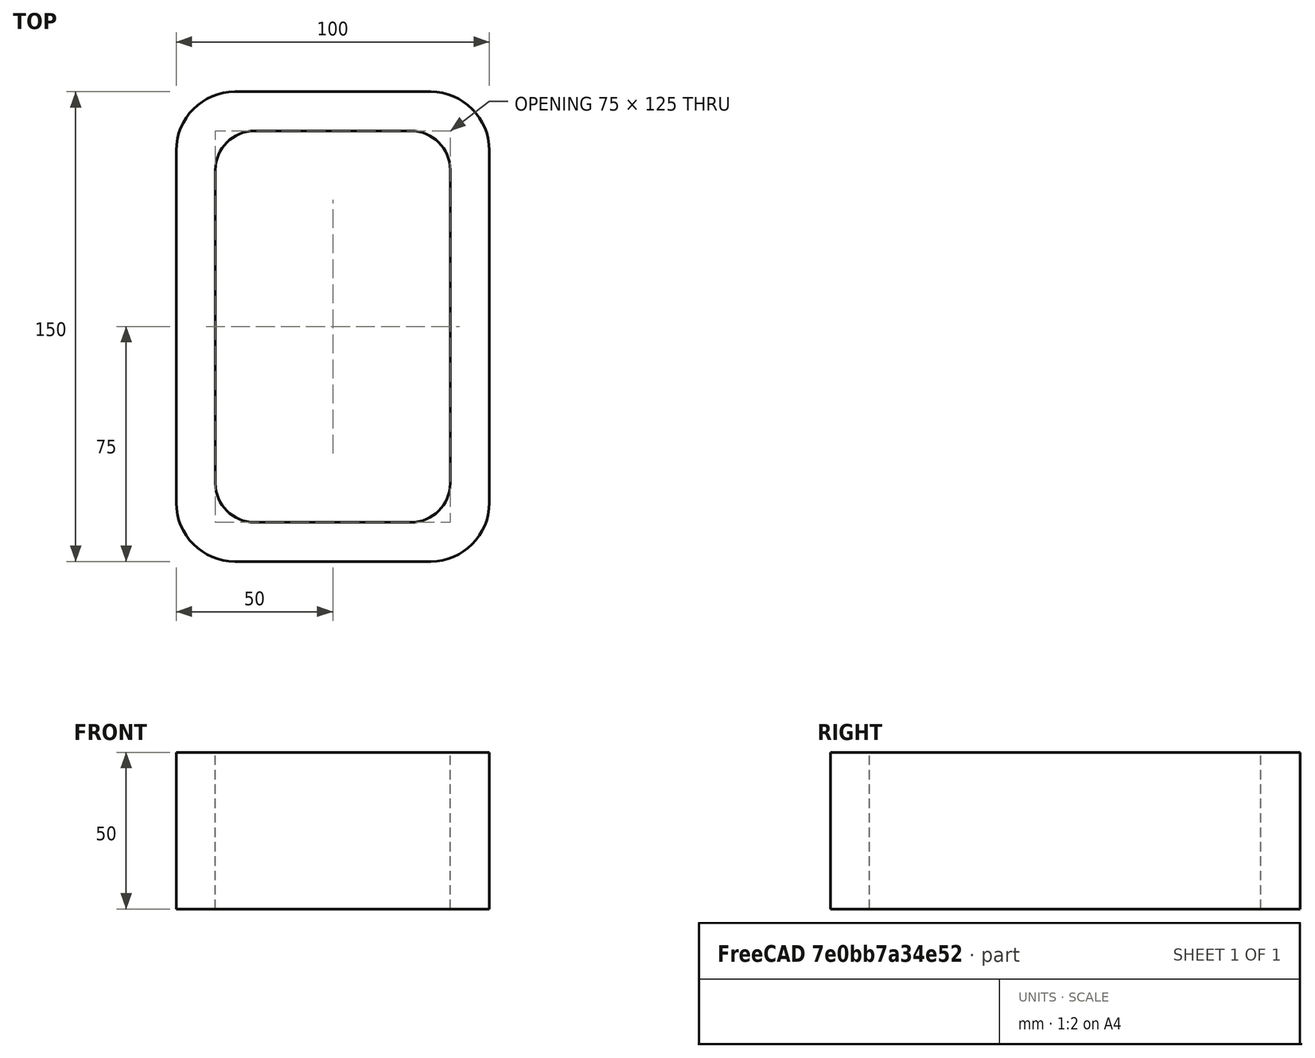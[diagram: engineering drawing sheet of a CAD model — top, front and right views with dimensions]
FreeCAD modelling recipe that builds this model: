
FCSTD DOCUMENT  (FreeCAD 0.15R4671 (Git))
Label: Rectangular hollow section 150x100x12.5 EN10219 S235JRH
License: All rights reserved
LicenseURL: http://en.wikipedia.org/wiki/All_rights_reserved
objects: Sketcher::SketchObject×1, Part::Extrusion×1
note: 2 computed .brp shape members not serialized (recipe doc carries the construction recipe); baked Part::Feature solids carry a one-line shape summary decoded from their .brp

FEATURE [Sketcher::SketchObject] Sketch
  sketch-geometry (16):
    g0: LineSegment StartX=-25 StartY=62.5 StartZ=0 EndX=25 EndY=62.5 EndZ=0
    g1: LineSegment StartX=37.5 StartY=50 StartZ=0 EndX=37.5 EndY=-50 EndZ=0
    g2: LineSegment StartX=25 StartY=-62.5 StartZ=0 EndX=-25 EndY=-62.5 EndZ=0
    g3: LineSegment StartX=-37.5 StartY=-50 StartZ=0 EndX=-37.5 EndY=50 EndZ=0
    g4: LineSegment StartX=-31.25 StartY=75 StartZ=0 EndX=31.25 EndY=75 EndZ=0
    g5: LineSegment StartX=50 StartY=56.25 StartZ=0 EndX=50 EndY=-56.25 EndZ=0
    g6: LineSegment StartX=31.25 StartY=-75 StartZ=0 EndX=-31.25 EndY=-75 EndZ=0
    g7: LineSegment StartX=-50 StartY=-56.25 StartZ=0 EndX=-50 EndY=56.25 EndZ=0
    g8: ArcOfCircle CenterX=-25 CenterY=50 CenterZ=0 NormalX=0 NormalY=0 NormalZ=1 Radius=12.5 StartAngle=1.5708 EndAngle=3.14159
    g9: ArcOfCircle CenterX=25 CenterY=50 CenterZ=0 NormalX=0 NormalY=0 NormalZ=1 Radius=12.5 StartAngle=0 EndAngle=1.5708
    g10: ArcOfCircle CenterX=25 CenterY=-50 CenterZ=0 NormalX=0 NormalY=0 NormalZ=1 Radius=12.5 StartAngle=4.71239 EndAngle=6.28319
    g11: ArcOfCircle CenterX=-25 CenterY=-50 CenterZ=0 NormalX=0 NormalY=0 NormalZ=1 Radius=12.5 StartAngle=3.14159 EndAngle=4.71239
    g12: ArcOfCircle CenterX=31.25 CenterY=56.25 CenterZ=0 NormalX=0 NormalY=0 NormalZ=1 Radius=18.75 StartAngle=0 EndAngle=1.5708
    g13: ArcOfCircle CenterX=31.25 CenterY=-56.25 CenterZ=0 NormalX=0 NormalY=0 NormalZ=1 Radius=18.75 StartAngle=4.71239 EndAngle=6.28319
    g14: ArcOfCircle CenterX=-31.25 CenterY=-56.25 CenterZ=0 NormalX=0 NormalY=0 NormalZ=1 Radius=18.75 StartAngle=3.14159 EndAngle=4.71239
    g15: ArcOfCircle CenterX=-31.25 CenterY=56.25 CenterZ=0 NormalX=0 NormalY=0 NormalZ=1 Radius=18.75 StartAngle=1.5708 EndAngle=3.14159
  constraints (36):
    c: Horizontal(g2)
    c: Vertical(g3)
    c: Horizontal(g6)
    c: Vertical(g7)
    c: Tangent(g3,g8) = 1.5708
    c: Tangent(g0,g8) = 1.5708
    c: Tangent(g0,g9) = 1.5708
    c: Tangent(g1,g9) = 1.5708
    c: Tangent(g1,g10) = 1.5708
    c: Tangent(g2,g10) = 1.5708
    c: Tangent(g2,g11) = 1.5708
    c: Tangent(g3,g11) = 1.5708
    c: Tangent(g4,g12) = 1.5708
    c: Tangent(g5,g12) = 1.5708
    c: Tangent(g5,g13) = 1.5708
    c: Tangent(g6,g13) = 1.5708
    c: Tangent(g6,g14) = 1.5708
    c: Tangent(g7,g14) = 1.5708
    c: Tangent(g7,g15) = 1.5708
    c: Tangent(g4,g15) = 1.5708
    c: Equal(g9,g8)
    c: Equal(g9,g11)
    c: Equal(g9,g10)
    c: Equal(g12,g15)
    c: Equal(g12,g14)
    c: Equal(g12,g13)
    c: Symmetric(g4,g6,g-1)
    c: Symmetric(g7,g5,g-2)
    c: DistanceY(g4,g6) = -150
    c: DistanceX(g7,g5) = 100
    c: Symmetric(g3,g1,g-2)
    c: Symmetric(g0,g2,g-1)
    c: DistanceY(g0,g4) = 12.5
    c: DistanceX(g5,g1) = -12.5
    c: Radius(g9) = 12.5
    c: Radius(g12) = 18.75
FEATURE [Part::Extrusion] Extrude  label="Rectangular hollow section 150x100x12.5 EN10219 S235JRH"
  Base = -> Sketch
  Dir = (0,0,50)
  Solid = true
